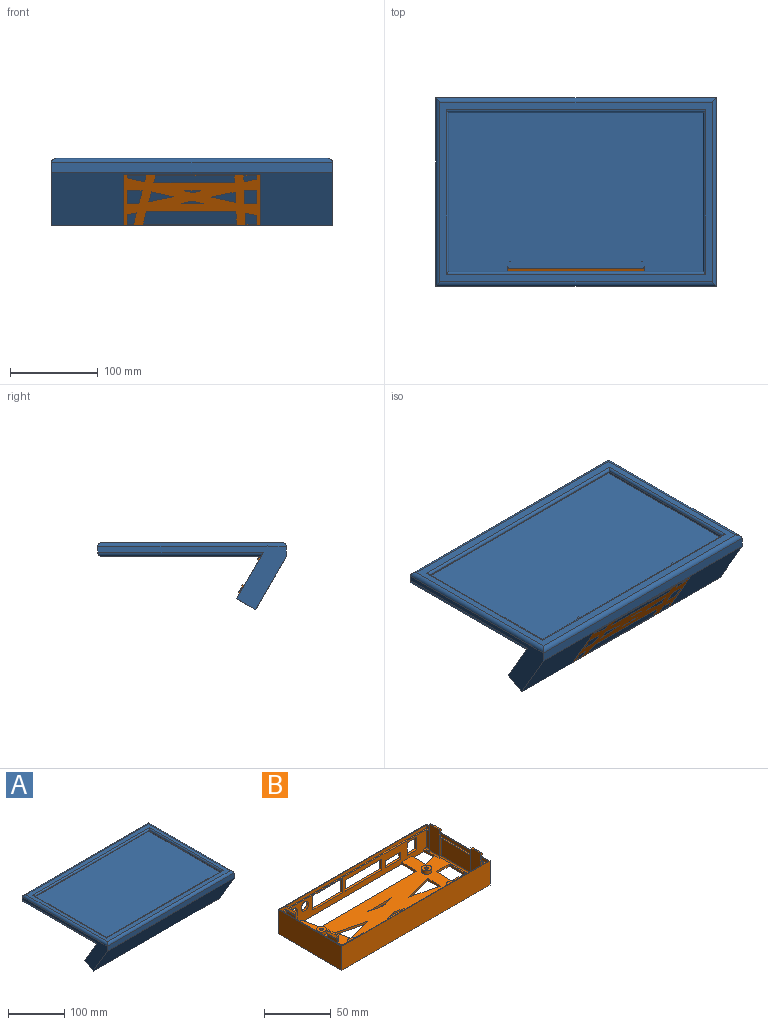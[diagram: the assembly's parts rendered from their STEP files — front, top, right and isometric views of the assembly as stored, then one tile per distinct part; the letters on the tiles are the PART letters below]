
ASSEMBLY  parts=2 mates=3
PART A: 33 faces, bbox 320x215x76.6 mm
  f0: plane 300x196.34mm, normal (0,0,1), area 58901.9mm2, adj f11,f13,f14,f30
  f1: plane 215x71.62mm, normal (1,0,0), area 2996.7mm2, adj f2,f4,f16,f17,f18,f19,f27
  f2: plane 320x6mm, normal (0,1,0), area 1920mm2, adj f1,f3,f21,f28
  f3: plane 215x73.12mm, normal (-1,0,0), area 2999.3mm2, adj f2,f4,f16,f17,f18,f22,f29,f31
  f4: plane 320x11mm, normal (0,-1,0), area 3520mm2, adj f1,f3,f17,f20
  f5: plane 310x205mm, normal (0,0,1), area 8198mm2, adj f19,f20,f21,f22,f23,f24,f25,f26
  f6: plane 310x181.13mm, normal (0,0,-1), area 56151.1mm2, adj f16,f27,f28,f29
  f7: plane 181x0.3mm, normal (1,0,0), area 54.3mm2, adj f8,f10,f15,f23
  f8: plane 290x0.3mm, normal (0,1,0), area 87mm2, adj f7,f9,f15,f25
  f9: plane 181x0.3mm, normal (-1,0,0), area 54.3mm2, adj f8,f10,f15,f26
  f10: plane 290x0.3mm, normal (0,-1,0), area 87mm2, adj f7,f9,f15,f24
  f11: plane 196.34x7.7mm, normal (1,0,0), area 1502mm2, adj f0,f12,f14,f15,f30
  f12: plane 300x6.93mm, normal (0,1,0), area 2077.9mm2, adj f11,f13,f15,f30
  f13: plane 196.34x7.7mm, normal (-1,0,0), area 1502mm2, adj f0,f12,f14,f15,f30
  f14: plane 300x7.7mm, normal (0,-1,0), area 2310mm2, adj f0,f11,f13,f15
  f15: plane 300x195mm, normal (0,0,-1), area 6010mm2, adj f7,f8,f9,f10,f11,f12,f13,f14
  f16: plane 320x53.12mm, normal (0,0.87,0.5), area 17793.6mm2, adj f1,f3,f6,f18,f27,f29
  f17: plane 320x60.62mm, normal (0,-0.87,-0.5), area 22400mm2, adj f1,f3,f4,f18
  f18: plane 320x21.65mm, normal (0,0.5,-0.87), area 8000mm2, adj f1,f3,f16,f17
  f19: cylinder r=5mm len=215mm, axis (0,-1,0), area 1660.1mm2, adj f1,f5,f20,f21
  f20: cylinder r=5mm len=320mm, axis (-1,0,0), area 2484.7mm2, adj f4,f5,f19,f22
  f21: cylinder r=5mm len=320mm, axis (1,0,0), area 2484.7mm2, adj f2,f5,f19,f22
  f22: cylinder r=5mm len=215mm, axis (0,1,0), area 1657.4mm2, adj f3,f5,f20,f21,f31,f32
  f23: cylinder r=3mm len=187mm, axis (0,1,0), area 863.2mm2, adj f5,f7,f24,f25
  f24: cylinder r=3mm len=296mm, axis (1,0,0), area 1376.9mm2, adj f5,f10,f23,f26
  f25: cylinder r=3mm len=296mm, axis (-1,0,0), area 1376.9mm2, adj f5,f8,f23,f26
  f26: cylinder r=3mm len=187mm, axis (0,-1,0), area 863.2mm2, adj f5,f9,f24,f25
  f27: cylinder r=5mm len=189.02mm, axis (0,1,0), area 1455.8mm2, adj f1,f6,f16,f28
  f28: cylinder r=5mm len=320mm, axis (-1,0,0), area 2484.7mm2, adj f2,f6,f27,f29
  f29: cylinder r=5mm len=189.02mm, axis (0,-1,0), area 1455.8mm2, adj f3,f6,f16,f28
  f30: plane 300x1.34mm, normal (0,0.5,-0.87), area 464.1mm2, adj f0,f11,f12,f13
  f31: plane 1.51x0.88mm, normal (0,0.87,0.5), area 0.1mm2, adj f3,f22,f32
  f32: plane 2.6x1.5mm, normal (0,-0.5,0.87), area 0.2mm2, adj f3,f22,f31
PART B: 161 faces, bbox 156.4x67.5x27 mm
  f0: plane 150x63.5mm, normal (0,0,1), area 5371.1mm2, adj f10,f12,f58,f59,f61,f62,f80,f81
  f1: plane 3.8x1.2mm, normal (0,0,1), area 4.6mm2, adj f10,f79,f95,f123
  f2: plane 3.8x1.2mm, normal (0,0,1), area 4.6mm2, adj f12,f60,f98,f127
  f3: plane 3.8x1.2mm, normal (0,0,1), area 4.6mm2, adj f12,f57,f101,f129
  f4: plane 156.4x67.5mm, normal (0,0,-1), area 6655.4mm2, adj f10,f12,f14,f15,f16,f17,f123,f124
  f5: plane 15.8x3.8mm, normal (-1,0,0), area 60mm2, adj f10,f40,f93,f95
  f6: plane 15.8x3.8mm, normal (1,0,0), area 60mm2, adj f10,f40,f90,f92
  f7: plane 31.1x15.8mm, normal (1,0,0), area 491.4mm2, adj f40,f102,f103,f106
  f8: plane 15.8x3.8mm, normal (-1,0,0), area 60mm2, adj f12,f40,f96,f98
  f9: plane 15.8x3.8mm, normal (1,0,0), area 60mm2, adj f12,f40,f99,f101
  f10: plane 152.4x19mm, normal (0,1,0), area 2841.8mm2, adj f0,f1,f4,f5,f6,f40,f92,f95
  f11: plane 31.1x15.8mm, normal (-1,0,0), area 491.4mm2, adj f40,f85,f87,f89
  f12: plane 152.4x19mm, normal (0,-1,0), area 1727.8mm2, adj f0,f2,f3,f4,f8,f9,f18,f19
  f13: plane 156.4x67.5mm, normal (0,0,1), area 355.7mm2, adj f14,f15,f16,f17,f36,f37,f38,f39
  f14: plane 67.5x22mm, normal (-1,0,0), area 1485mm2, adj f4,f13,f15,f17
  f15: plane 156.4x22mm, normal (0,-1,0), area 3440.8mm2, adj f4,f13,f14,f16
  f16: plane 67.5x22mm, normal (1,0,0), area 1485mm2, adj f4,f13,f15,f17
  f17: plane 156.4x22mm, normal (0,1,0), area 2326.8mm2, adj f4,f13,f14,f16,f18,f19,f20,f21
  f18: cylinder r=4mm len=8mm, axis (0,1,0), area 50.3mm2, adj f12,f17
  f19: cylinder r=4mm len=8mm, axis (0,1,0), area 50.3mm2, adj f12,f17
  f20: plane 13x2mm, normal (-1,0,0), area 26mm2, adj f12,f17,f21,f23
  f21: plane 31.5x2mm, normal (0,0,1), area 63mm2, adj f12,f17,f20,f22
  f22: plane 13x2mm, normal (1,0,0), area 26mm2, adj f12,f17,f21,f23
  f23: plane 31.5x2mm, normal (0,0,-1), area 63mm2, adj f12,f17,f20,f22
  f24: plane 10x2mm, normal (-1,0,0), area 20mm2, adj f12,f17,f25,f27
  f25: plane 38.5x2mm, normal (0,0,1), area 77mm2, adj f12,f17,f24,f26
  f26: plane 10x2mm, normal (1,0,0), area 20mm2, adj f12,f17,f25,f27
  f27: plane 38.5x2mm, normal (0,0,-1), area 77mm2, adj f12,f17,f24,f26
  f28: plane 6.5x2mm, normal (-1,0,0), area 13mm2, adj f12,f17,f29,f31
  f29: plane 16x2mm, normal (0,0,1), area 32mm2, adj f12,f17,f28,f30
  f30: plane 6.5x2mm, normal (1,0,0), area 13mm2, adj f12,f17,f29,f31
  f31: plane 16x2mm, normal (0,0,-1), area 32mm2, adj f12,f17,f28,f30
  f32: plane 11.5x2mm, normal (-1,0,0), area 23mm2, adj f12,f17,f33,f35
  f33: plane 10x2mm, normal (0,0,1), area 20mm2, adj f12,f17,f32,f34
  f34: plane 11.5x2mm, normal (1,0,0), area 23mm2, adj f12,f17,f33,f35
  f35: plane 10x2mm, normal (0,0,-1), area 20mm2, adj f12,f17,f32,f34
  f36: plane 154.8x3mm, normal (0,-1,0), area 464.4mm2, adj f13,f37,f39,f40
  f37: plane 65.9x3mm, normal (1,0,0), area 197.7mm2, adj f13,f36,f38,f40
  f38: plane 154.8x3mm, normal (0,1,0), area 464.4mm2, adj f13,f37,f39,f40
  f39: plane 65.9x3mm, normal (-1,0,0), area 197.7mm2, adj f13,f36,f38,f40
  f40: plane 154.8x65.9mm, normal (0,0,1), area 526.4mm2, adj f5,f6,f7,f8,f9,f10,f11,f12
  f41: plane 10x5.77mm, normal (1,0,0), area 57.7mm2, adj f40,f42,f47,f48
  f42: plane 10x1.2mm, normal (0,0,-1), area 12mm2, adj f41,f43,f47,f48
  f43: plane 10x0.8mm, normal (1,0,0), area 8mm2, adj f42,f44,f47,f48
  f44: plane 10x1.43mm, normal (0.77,0,0.64), area 18.7mm2, adj f43,f45,f47,f48
  f45: plane 10x1.2mm, normal (0,0,1), area 12mm2, adj f44,f46,f47,f48
  f46: plane 23.8x10mm, normal (-1,0,0), area 238mm2, adj f45,f47,f48,f62,f85,f96
  f47: plane 8x2.4mm, normal (0,1,0), area 11.4mm2, adj f40,f41,f42,f43,f44,f45,f46
  f48: plane 8x2.4mm, normal (0,-1,0), area 11.4mm2, adj f40,f41,f42,f43,f44,f45,f46
  f49: plane 10x5.77mm, normal (-1,0,0), area 57.7mm2, adj f40,f50,f55,f56
  f50: plane 10x1.2mm, normal (0,0,-1), area 12mm2, adj f49,f54,f55,f56
  f51: plane 23.8x10mm, normal (1,0,0), area 238mm2, adj f52,f55,f56,f59,f99,f102
  f52: plane 10x1.2mm, normal (0,0,1), area 12mm2, adj f51,f53,f55,f56
  f53: plane 10x1.43mm, normal (-0.77,0,0.64), area 18.7mm2, adj f52,f54,f55,f56
  f54: plane 10x0.8mm, normal (-1,0,0), area 8mm2, adj f50,f53,f55,f56
  f55: plane 8x2.4mm, normal (0,1,0), area 11.4mm2, adj f40,f49,f50,f51,f52,f53,f54
  f56: plane 8x2.4mm, normal (0,-1,0), area 11.4mm2, adj f40,f49,f50,f51,f52,f53,f54
  f57: cylinder r=1.2mm len=1.2mm, axis (-1,0,0), area 0.8mm2, adj f3,f59,f100
  f58: cylinder r=1.2mm len=1.2mm, axis (1,0,0), area 0.8mm2, adj f0,f59,f104
  f59: cylinder r=1.2mm len=12.4mm, axis (0,1,0), area 20.5mm2, adj f0,f51,f57,f58,f129
  f60: cylinder r=1.2mm len=1.2mm, axis (1,0,0), area 0.8mm2, adj f2,f62,f97
  f61: cylinder r=1.2mm len=1.2mm, axis (-1,0,0), area 0.8mm2, adj f0,f62,f86
  f62: cylinder r=1.2mm len=12.4mm, axis (0,1,0), area 20.5mm2, adj f0,f46,f60,f61,f127
  f63: plane 10x5.77mm, normal (-1,0,0), area 57.7mm2, adj f40,f64,f69,f70
  f64: plane 10x1.2mm, normal (0,0,-1), area 12mm2, adj f63,f65,f69,f70
  f65: plane 10x0.8mm, normal (-1,0,0), area 8mm2, adj f64,f66,f69,f70
  f66: plane 10x1.43mm, normal (-0.77,0,0.64), area 18.7mm2, adj f65,f67,f69,f70
  f67: plane 10x1.2mm, normal (0,0,1), area 12mm2, adj f66,f68,f69,f70
  f68: plane 23.8x10mm, normal (1,0,0), area 238mm2, adj f67,f69,f70,f84,f90,f103
  f69: plane 8x2.4mm, normal (0,-1,0), area 11.4mm2, adj f40,f63,f64,f65,f66,f67,f68
  f70: plane 8x2.4mm, normal (0,1,0), area 11.4mm2, adj f40,f63,f64,f65,f66,f67,f68
  f71: plane 10x1.2mm, normal (0,0,1), area 12mm2, adj f72,f76,f77,f78
  f72: plane 10x1.43mm, normal (0.77,0,0.64), area 18.7mm2, adj f71,f73,f77,f78
  f73: plane 10x0.8mm, normal (1,0,0), area 8mm2, adj f72,f74,f77,f78
  f74: plane 10x1.2mm, normal (0,0,-1), area 12mm2, adj f73,f75,f77,f78
  f75: plane 10x5.77mm, normal (1,0,0), area 57.7mm2, adj f40,f74,f77,f78
  f76: plane 23.8x10mm, normal (-1,0,0), area 238mm2, adj f71,f77,f78,f81,f89,f93
  f77: plane 8x2.4mm, normal (0,-1,0), area 11.4mm2, adj f40,f71,f72,f73,f74,f75,f76
  f78: plane 8x2.4mm, normal (0,1,0), area 11.4mm2, adj f40,f71,f72,f73,f74,f75,f76
  f79: cylinder r=1.2mm len=1.2mm, axis (1,0,0), area 0.8mm2, adj f1,f81,f94
  f80: cylinder r=1.2mm len=1.2mm, axis (-1,0,0), area 0.8mm2, adj f0,f81,f88
  f81: cylinder r=1.2mm len=12.4mm, axis (0,-1,0), area 20.5mm2, adj f0,f76,f79,f80,f123
  f82: cylinder r=1.2mm len=1.2mm, axis (1,0,0), area 0.8mm2, adj f0,f84,f91
  f83: cylinder r=1.2mm len=1.2mm, axis (-1,0,0), area 0.8mm2, adj f0,f84,f105
  f84: cylinder r=1.2mm len=12.4mm, axis (0,1,0), area 20.5mm2, adj f0,f68,f82,f83
  f85: cylinder r=1.2mm len=15.8mm, axis (0,0,-1), area 29.8mm2, adj f11,f40,f46,f86
  f86: sphere r=1.2mm, area 2.3mm2, adj f61,f85,f87
  f87: cylinder r=1.2mm len=31.1mm, axis (0,-1,0), area 58.6mm2, adj f0,f11,f86,f88
  f88: sphere r=1.2mm, area 2.3mm2, adj f80,f87,f89
  f89: cylinder r=1.2mm len=15.8mm, axis (0,0,1), area 29.8mm2, adj f11,f40,f76,f88
  f90: cylinder r=1.2mm len=15.8mm, axis (0,0,1), area 29.8mm2, adj f6,f40,f68,f91
  f91: sphere r=1.2mm, area 2.3mm2, adj f82,f90,f92
  f92: cylinder r=1.2mm len=3.8mm, axis (0,1,0), area 7.2mm2, adj f0,f6,f10,f91
  f93: cylinder r=1.2mm len=15.8mm, axis (0,0,-1), area 29.8mm2, adj f5,f40,f76,f94
  f94: sphere r=1.2mm, area 2.3mm2, adj f79,f93,f95
  f95: cylinder r=1.2mm len=3.8mm, axis (0,-1,0), area 7.2mm2, adj f1,f5,f10,f94
  f96: cylinder r=1.2mm len=15.8mm, axis (0,0,1), area 29.8mm2, adj f8,f40,f46,f97
  f97: sphere r=1.2mm, area 2.3mm2, adj f60,f96,f98
  f98: cylinder r=1.2mm len=3.8mm, axis (0,-1,0), area 7.2mm2, adj f2,f8,f12,f97
  f99: cylinder r=1.2mm len=15.8mm, axis (0,0,1), area 29.8mm2, adj f9,f40,f51,f100
  f100: sphere r=1.2mm, area 2.3mm2, adj f57,f99,f101
  f101: cylinder r=1.2mm len=3.8mm, axis (0,1,0), area 7.2mm2, adj f3,f9,f12,f100
  f102: cylinder r=1.2mm len=15.8mm, axis (0,0,-1), area 29.8mm2, adj f7,f40,f51,f104
  f103: cylinder r=1.2mm len=15.8mm, axis (0,0,-1), area 29.8mm2, adj f7,f40,f68,f105
  f104: sphere r=1.2mm, area 2.3mm2, adj f58,f102,f106
  f105: sphere r=1.2mm, area 2.3mm2, adj f83,f103,f106
  f106: cylinder r=1.2mm len=31.1mm, axis (0,1,0), area 58.6mm2, adj f0,f7,f104,f105
  f107: cylinder r=3.78mm len=7.55mm, axis (0,0,-1), area 71.2mm2, adj f0,f108
  f108: plane 7.55x7.55mm, normal (0,0,1), area 38.8mm2, adj f107,f110
  f109: plane 2.75x2.75mm, normal (0,0,1), area 5.9mm2, adj f110
  f110: cylinder r=1.38mm len=3.5mm, axis (0,0,1), area 30.2mm2, adj f108,f109
  f111: cylinder r=3.78mm len=7.55mm, axis (0,0,-1), area 71.2mm2, adj f0,f112
  f112: plane 7.55x7.55mm, normal (0,0,1), area 38.8mm2, adj f111,f114
  f113: plane 2.75x2.75mm, normal (0,0,1), area 5.9mm2, adj f114
  f114: cylinder r=1.38mm len=3.5mm, axis (0,0,1), area 30.2mm2, adj f112,f113
  f115: cylinder r=3.78mm len=7.55mm, axis (0,0,-1), area 71.2mm2, adj f0,f116
  f116: plane 7.55x7.55mm, normal (0,0,1), area 38.8mm2, adj f115,f118
  f117: plane 2.75x2.75mm, normal (0,0,1), area 5.9mm2, adj f118
  f118: cylinder r=1.38mm len=3.5mm, axis (0,0,1), area 30.2mm2, adj f116,f117
  f119: cylinder r=3.78mm len=7.55mm, axis (0,0,-1), area 71.2mm2, adj f0,f120
  f120: plane 7.55x7.55mm, normal (0,0,1), area 38.8mm2, adj f119,f122
  f121: plane 2.75x2.75mm, normal (0,0,1), area 5.9mm2, adj f122
  f122: cylinder r=1.38mm len=3.5mm, axis (0,0,1), area 30.2mm2, adj f120,f121
  f123: plane 4.17x2mm, normal (-1,0,0), area 8.3mm2, adj f1,f4,f10,f81,f124
  f124: plane 14.47x3.54mm, normal (-0.24,-0.97,0), area 29.8mm2, adj f0,f4,f123,f125
  f125: plane 7.71x2mm, normal (1,-0.04,0), area 15.4mm2, adj f0,f4,f10,f124
  f126: plane 12.97x3.38mm, normal (-0.25,0.97,0), area 26.8mm2, adj f0,f4,f127,f128
  f127: plane 11.09x2mm, normal (-1,0,0), area 22.2mm2, adj f2,f4,f12,f62,f126
  f128: plane 14.48x2mm, normal (1,-0.04,0), area 29mm2, adj f0,f4,f12,f126
  f129: plane 12.16x2mm, normal (1,0,0), area 24.3mm2, adj f3,f4,f12,f59,f130
  f130: plane 10.48x2.56mm, normal (0.24,0.97,0), area 21.6mm2, adj f0,f4,f129,f131
  f131: plane 14.72x3.27mm, normal (-0.98,-0.22,0), area 30.2mm2, adj f0,f4,f12,f130
  f132: plane 26.82x6.56mm, normal (0.24,0.97,0), area 55.2mm2, adj f0,f4,f133,f134
  f133: plane 13.69x2mm, normal (-1,0.04,0), area 27.4mm2, adj f0,f4,f132,f134
  f134: plane 27.32x7.13mm, normal (0.25,-0.97,0), area 56.5mm2, adj f0,f4,f132,f133
  f135: plane 12.67x3.1mm, normal (0.24,0.97,0), area 26.1mm2, adj f0,f4,f136,f137
  f136: plane 12.31x3.21mm, normal (-0.25,0.97,0), area 25.4mm2, adj f0,f4,f135,f137
  f137: plane 24.98x2mm, normal (0,-1,0), area 50mm2, adj f0,f4,f135,f136
  f138: plane 27.45x6.71mm, normal (-0.24,-0.97,0), area 56.5mm2, adj f0,f4,f139,f140
  f139: plane 13.12x2.91mm, normal (0.98,0.22,0), area 26.9mm2, adj f0,f4,f138,f140
  f140: plane 24.54x6.4mm, normal (-0.25,0.97,0), area 50.7mm2, adj f0,f4,f138,f139
  f141: plane 16.17x2mm, normal (1,0,0), area 32.3mm2, adj f0,f4,f142,f144
  f142: plane 16.9x2mm, normal (0,1,0), area 33.8mm2, adj f0,f4,f141,f143
  f143: plane 16.23x3.61mm, normal (-0.98,-0.22,0), area 33.3mm2, adj f0,f4,f142,f144
  f144: plane 13.29x2mm, normal (0,-1,0), area 26.6mm2, adj f0,f4,f141,f143
  f145: plane 16.61x3.69mm, normal (0.98,0.22,0), area 34mm2, adj f0,f4,f12,f146
  f146: plane 101.91x2mm, normal (0,1,0), area 203.8mm2, adj f0,f4,f145,f147
  f147: plane 16.15x2mm, normal (-1,0.04,0), area 32.3mm2, adj f0,f4,f12,f146
  f148: plane 14.03x2mm, normal (0,1,0), area 28.1mm2, adj f0,f4,f149,f151
  f149: plane 16.83x2mm, normal (-1,0,0), area 33.7mm2, adj f0,f4,f148,f150
  f150: plane 13.42x2mm, normal (0,-1,0), area 26.8mm2, adj f0,f4,f149,f151
  f151: plane 16.77x2mm, normal (1,-0.04,0), area 33.6mm2, adj f0,f4,f148,f150
  f152: plane 9.24x2.26mm, normal (-0.24,-0.97,0), area 19mm2, adj f0,f4,f153,f154
  f153: plane 8.66x2.26mm, normal (0.25,-0.97,0), area 17.9mm2, adj f0,f4,f152,f154
  f154: plane 17.91x2mm, normal (0,1,0), area 35.8mm2, adj f0,f4,f152,f153
  f155: plane 2.79x2mm, normal (1,0,0), area 5.6mm2, adj f0,f4,f10,f157
  f156: plane 7.89x2mm, normal (-0.98,-0.22,0), area 16.2mm2, adj f0,f4,f10,f157
  f157: plane 19.56x5.1mm, normal (0.25,-0.97,0), area 40.4mm2, adj f0,f4,f155,f156
  f158: plane 92.13x2mm, normal (0,-1,0), area 184.3mm2, adj f0,f4,f159,f160
  f159: plane 9.13x2.03mm, normal (0.98,0.22,0), area 18.7mm2, adj f0,f4,f10,f158
  f160: plane 9.13x2mm, normal (-1,0.04,0), area 18.3mm2, adj f0,f4,f10,f158
PLACE A t=(-686.6,-104.21,108.03)mm
PLACE B rot(axis=(-1,0,0),60deg) t=(-692.04,-126.46,64.01)mm
MATE planar A.f17 <-> B.f4  axis (0,-0.87,-0.5) through (-687.69,-134.37,77.72)mm
MATE planar B.f17 <-> A.f18  axis (0,0.5,-0.87) through (-638.24,-106.65,53.31)mm
MATE fastened A.f18 <-> B.f17  axis (0,0.5,-0.87) through (-687.69,-116.87,47.41)mm
